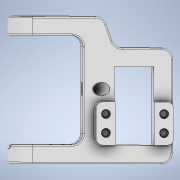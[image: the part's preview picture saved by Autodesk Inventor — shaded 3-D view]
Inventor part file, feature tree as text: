
AUTODESK INVENTOR PART (.ipt)
format: ipt  version: 2020.3 (Build 243373000, 373)  size: 539,648 bytes
history: native  units: mm
features: fillet x11, sketch x8, extrude x6, hole x5, plane x2, chamfer x1
ambient origin geometry x8: Origin, YZ Plane, XZ Plane, XY Plane, X Axis, Y Axis, Z Axis, Center Point
bodies: Solid1 (feature_tree)
feature tree (33):
  sketch  "Sketch1"  dims[d4=24.6mm d5=12.4mm]
  extrude  "Extrusion1"  Depth=12.4mm
  hole  "Hole1"  [1 undecoded]
  fillet  "Fillet1"  Radius=23.5mm
  fillet  "Fillet2"  Radius=34.5mm
  sketch  "Sketch2"  dims[d9=6.0mm d11=10.0mm d12=23.5mm d14=34.5mm]
  hole  "Hole2"  [1 undecoded]
  sketch  "Sketch8"  dims[d19=1.9mm d20=6.0mm d21=4.0mm d22=2.0mm d23=90.0deg d24=10.0mm d25=20.594885mm]
  extrude  "Extrusion3"  Depth=6.0mm
  extrude  "Extrusion4"  Depth=3.7mm
  hole  "Hole5"  [1 undecoded]
  fillet  "Fillet4"  Radius=10.0mm
  fillet  "Fillet9"  Radius=3.5mm
  fillet  "Fillet10"  Radius=0.5mm
  fillet  "Fillet5"  Radius=0.5mm
  fillet  "Fillet6"  Radius=28.4mm
  hole  "Hole4"  [1 undecoded]
  fillet  "Fillet11"  Radius=6.0mm
  extrude  "Extrusion6"  Depth=2.0mm
  plane  "Work Plane1"
  extrude  "Extrusion7"  Depth=0.5mm
  fillet  "Fillet12"  Radius=2.0mm
  hole  "Hole6"  [1 undecoded]
  plane  "Work Plane3"
  extrude  "Extrusion8"  Depth=2.0mm
  chamfer  "Chamfer1"  Distance=0.3mm
  fillet  "Fillet13"  Radius=0.2mm
  fillet  "Fillet14"  [1 undecoded]
  sketch  "Sketch3"  dims[d16=6.0mm d17=15.0mm d18=0.0mm]
  sketch  "Sketch9"  dims[d27=8.8mm d28=6.0mm d29=4.0mm d30=2.0mm d31=90.0deg d32=8.0mm d33=20.594885mm d34=6.0mm]
  sketch  "Sketch10"  dims[d37=7.2mm d38=3.7mm]
  sketch  "Sketch11"  dims[d39=12.1mm d40=3.5mm d41=0.0mm d42=10.0mm d43=0.0mm d53=3.5mm d54=0.5mm d55=0.5mm d57=28.4mm]
  sketch  "Sketch12"  dims[d58=6.8mm d59=20.92mm d60=0.0mm d61=6.0mm d62=3.0mm d63=6.0mm d64=4.0mm d65=2.0mm d66=90.0deg d67=4.3mm d68=0.0mm d70=2.0mm d71=0.5mm d72=2.0mm d74=2.0mm d75=2.0mm d76=1.0mm d77=6.0mm d78=4.0mm d79=2.0mm d80=90.0deg d81=8.0mm d82=20.594885mm d83=0.3mm d84=0.2mm d85=0.0mm d86=0.0mm d87=1.0mm d88=3.5mm d89=-9.075712mm d90=4.0mm d91=4.0mm d92=1.0mm d93=33.941mm d94=0.0mm d95=0.2mm d96=2.1mm d97=6.0mm d98=4.0mm d99=2.0mm d100=90.0deg d101=7.3mm d102=0.0mm d103=24.0mm d104=7.0mm d105=7.0mm d106=0.0mm d107=0.2mm d108=0.8mm d109=45.0deg d110=1.0mm d111=2.0mm d112=3.490659mm]
note: 6 required parameter values undecoded (feature->parameter linkage not recoverable at this tier; creation-order binding heuristic only, values carry confidence <= 0.55)
